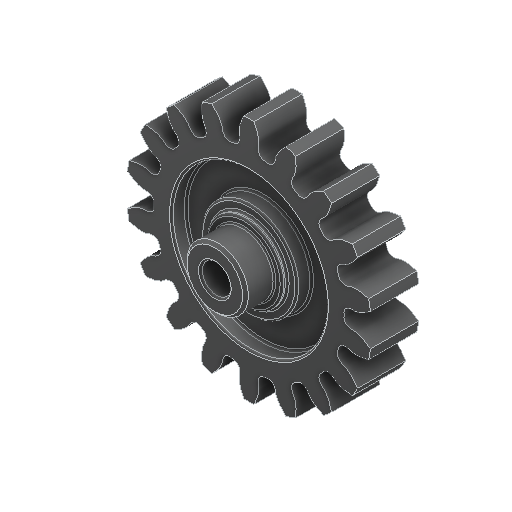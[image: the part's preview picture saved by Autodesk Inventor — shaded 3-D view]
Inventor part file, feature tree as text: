
AUTODESK INVENTOR PART (.ipt)
format: ipt  version: 2024.1 (Build 281209000, 209)  size: 429,568 bytes
history: native  units: in
note: dims shown in document units (in); Inventor stores cm internally (conversion verified against a paired STEP export)
features: chamfer x1
ambient origin geometry x8: Origin, YZ Plane, XZ Plane, XY Plane, X Axis, Y Axis, Z Axis, Center Point
bodies: Solid1 (feature_tree)
feature tree (1):
  chamfer  "Chamfer4"  [1 undecoded]
note: 1 required parameter value undecoded (feature->parameter linkage not recoverable at this tier; creation-order binding heuristic only, values carry confidence <= 0.55)
